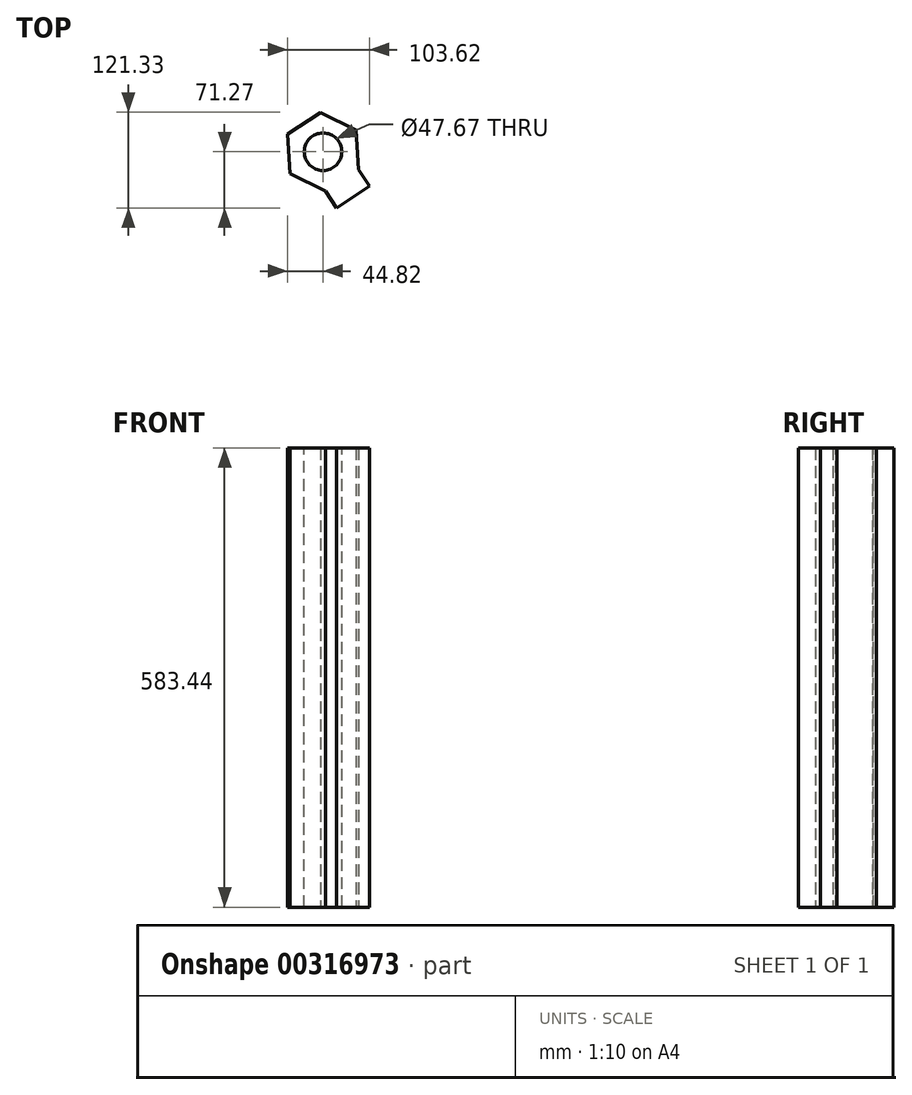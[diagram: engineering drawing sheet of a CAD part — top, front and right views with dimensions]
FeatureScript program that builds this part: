
annotation { "Feature Type Name" : "Feature", "Feature Type Description" : "" }
export const myFeature = defineFeature(function(context is Context, id is Id, definition is map)
    precondition{}
    {
        {
            var Q0;
            Q0=qCreatedBy(makeId("Top.planeOp"),FACE);
            var sketch = newSketch(context, id + "F0", { "sketchPlane" : qUnion([Q0])});
            skCircle(sketch, "E0.cCircle", {"center": v(0, 0) * mm, "radius": 43.42 * mm, "construction": true});
            skLineSegment(sketch, "E0.0", {"start": v(44.82, -22.47) * mm, "end": v(2.95, -50.06) * mm});
            skLineSegment(sketch, "E0.1", {"start": v(2.95, -50.06) * mm, "end": v(-41.87, -27.58) * mm});
            skLineSegment(sketch, "E0.2", {"start": v(-41.87, -27.58) * mm, "end": v(-44.82, 22.47) * mm});
            skLineSegment(sketch, "E0.3", {"start": v(-44.82, 22.47) * mm, "end": v(-2.95, 50.06) * mm});
            skLineSegment(sketch, "E0.4", {"start": v(-2.95, 50.06) * mm, "end": v(41.87, 27.58) * mm});
            skLineSegment(sketch, "E0.5", {"start": v(41.87, 27.58) * mm, "end": v(44.82, -22.47) * mm});
            skPoint(sketch, "E0.0.midPoint", {"position": v(23.89, -36.26) * mm});
            skSolve(sketch);
        }
        {
            var Q0;
            Q0=makeQuery(id+"F0.imprint","IMPRINT",FACE,{"disambiguationData":[TD([[makeQuery(id+"F0.imprint","IMPRINT",EDGE,{"derivedFrom":sQuery(id+"F0.wireOp",EDGE,"E0.0")}),-1.0]])]});
            extrude(context, id + "F1", {"entities" : qUnion([Q0]), "depth" : 583.44 * mm});
        }
        {
            var Q0;
            Q0=makeQuery(id+"F1.opExtrude","SWEPT_FACE",FACE,{"disambiguationData":[OSD([sQuery(id+"F0.wireOp",EDGE,"E0.0")])]});
            extrude(context, id + "F2", {"entities" : qUnion([Q0]), "operationType" : NewBodyOperationType.ADD, "depth" : 25.4 * mm});
        }
        {
            var Q0;
            {var subQ0=sQuery(id+"F0.wireOp",EDGE,"E0.0");Q0=makeQuery(id+"F2.boolean.opBoolean","MERGE",FACE,{"derivedFrom":[makeQuery(id+"F1.opExtrude","CAP_FACE",FACE,{"disambiguationData":[OSD([subQ0,sQuery(id+"F0.wireOp",EDGE,"E0.1"),sQuery(id+"F0.wireOp",EDGE,"E0.2"),sQuery(id+"F0.wireOp",EDGE,"E0.3"),sQuery(id+"F0.wireOp",EDGE,"E0.4"),sQuery(id+"F0.wireOp",EDGE,"E0.5")])],"isStart":false}),makeQuery(id+"F2.opExtrude","SWEPT_FACE",FACE,{"disambiguationData":[OSD([subQ0]),TDD([makeQuery(id+"F1.opExtrude","CAP_EDGE",EDGE,{"disambiguationData":[OSD([subQ0])],"isStart":false})])]})]});}
            var sketch = newSketch(context, id + "F3", { "sketchPlane" : qUnion([Q0])});
            skCircle(sketch, "E1", {"center": v(0, 0) * mm, "radius": 23.83 * mm});
            skSolve(sketch);
        }
        {
            var Q0;
            Q0=makeQuery(id+"F3.imprint","IMPRINT",FACE,{"disambiguationData":[TD([[makeQuery(id+"F3.imprint","IMPRINT",EDGE,{"derivedFrom":sQuery(id+"F3.wireOp",EDGE,"E1")}),1.0]])]});
            var Q1;
            Q1=sQuery(id+"F3.wireOp",EDGE,"E1");
            extrude(context, id + "F4", {"entities" : qUnion([Q0]), "operationType" : NewBodyOperationType.REMOVE, "surfaceEntities" : qUnion([Q1]), "oppositeDirection" : true, "depth" : 899.16 * mm});
        }
    });
